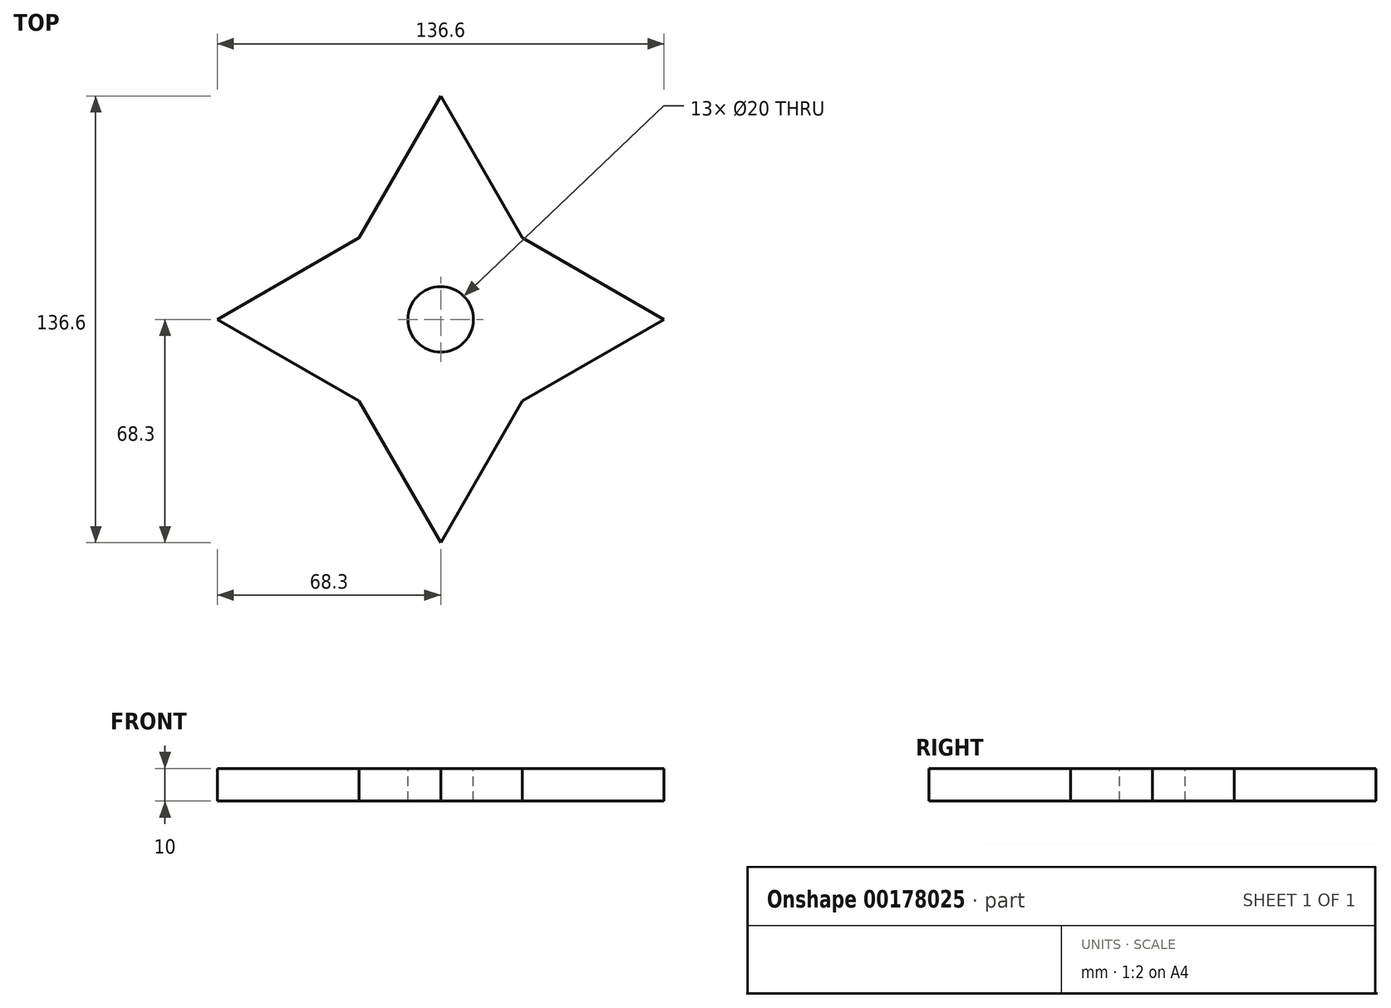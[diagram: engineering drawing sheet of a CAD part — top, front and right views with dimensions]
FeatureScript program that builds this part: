
annotation { "Feature Type Name" : "Feature", "Feature Type Description" : "" }
export const myFeature = defineFeature(function(context is Context, id is Id, definition is map)
    precondition{}
    {
        {
            var Q0;
            Q0=qCreatedBy(makeId("Top.planeOp"),FACE);
            var sketch = newSketch(context, id + "F0", { "sketchPlane" : qUnion([Q0])});
            skLineSegment(sketch, "E0.bottom", {"start": v(25, 25) * mm, "end": v(-25, 25) * mm});
            skLineSegment(sketch, "E0.top", {"start": v(25, -25) * mm, "end": v(-25, -25) * mm});
            skLineSegment(sketch, "E0.left", {"start": v(25, 25) * mm, "end": v(25, -25) * mm});
            skLineSegment(sketch, "E0.right", {"start": v(-25, 25) * mm, "end": v(-25, -25) * mm});
            skPoint(sketch, "E0.middle", {"position": v(0, 0) * mm});
            skLineSegment(sketch, "E1", {"start": v(0, 0) * mm, "end": v(0, 25) * mm, "construction": true});
            skLineSegment(sketch, "E2", {"start": v(-25, 25) * mm, "end": v(0, 68.3) * mm});
            skLineSegment(sketch, "E3.MirrorCS", {"start": v(25, 25) * mm, "end": v(0, 68.3) * mm});
            skLineSegment(sketch, "E4.1.0", {"start": v(-25, 25) * mm, "end": v(-68.3, 0) * mm});
            skLineSegment(sketch, "E4.1.1", {"start": v(-25, -25) * mm, "end": v(-68.3, 0) * mm});
            skLineSegment(sketch, "E4.2.0", {"start": v(-25, -25) * mm, "end": v(0, -68.3) * mm});
            skLineSegment(sketch, "E4.2.1", {"start": v(25, -25) * mm, "end": v(0, -68.3) * mm});
            skLineSegment(sketch, "E4.3.0", {"start": v(25, -25) * mm, "end": v(68.3, 0) * mm});
            skLineSegment(sketch, "E4.3.1", {"start": v(25, 25) * mm, "end": v(68.3, 0) * mm});
            skSolve(sketch);
        }
        {
            var Q0;
            Q0 = qSketchRegion(id + "F0", true);
            extrude(context, id + "F1", {"entities" : qUnion([Q0]), "depth" : 5 * mm, "hasSecondDirection" : true, "secondDirectionOppositeDirection" : true, "secondDirectionDepth" : 5 * mm});
        }
        {
            var Q0;
            Q0=makeQuery(id+"F1.opExtrude","CAP_FACE",FACE,{"disambiguationData":[OSD([sQuery(id+"F0.wireOp",EDGE,"E2"),sQuery(id+"F0.wireOp",EDGE,"E3.MirrorCS"),sQuery(id+"F0.wireOp",EDGE,"E4.1.0"),sQuery(id+"F0.wireOp",EDGE,"E4.1.1"),sQuery(id+"F0.wireOp",EDGE,"E4.2.0"),sQuery(id+"F0.wireOp",EDGE,"E4.2.1"),sQuery(id+"F0.wireOp",EDGE,"E4.3.0"),sQuery(id+"F0.wireOp",EDGE,"E4.3.1")])],"isStart":false});
            var sketch = newSketch(context, id + "F2", { "sketchPlane" : qUnion([Q0])});
            skCircle(sketch, "E5", {"center": v(0, 0) * mm, "radius": 10 * mm});
            skSolve(sketch);
        }
        {
            var Q0;
            Q0 = qSketchRegion(id + "F2", true);
            extrude(context, id + "F3", {"entities" : qUnion([Q0]), "operationType" : NewBodyOperationType.REMOVE, "endBound" : BoundingType.THROUGH_ALL, "oppositeDirection" : true, "depth" : 25 * mm});
        }
    });
